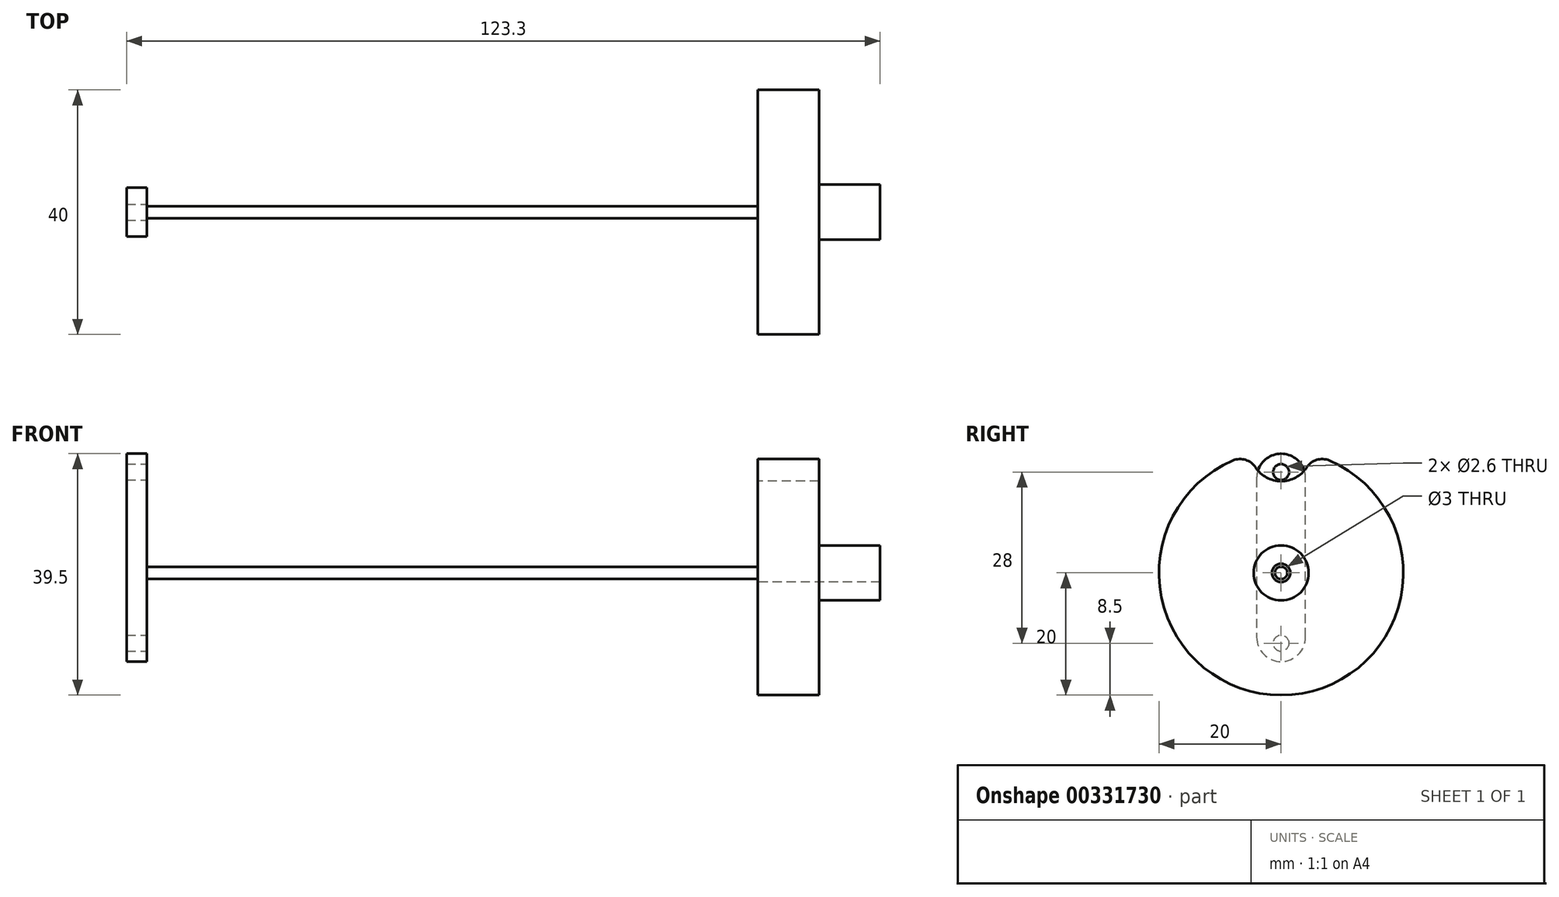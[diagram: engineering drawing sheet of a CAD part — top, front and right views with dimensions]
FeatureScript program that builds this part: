
annotation { "Feature Type Name" : "Feature", "Feature Type Description" : "" }
export const myFeature = defineFeature(function(context is Context, id is Id, definition is map)
    precondition{}
    {
        {
            var Q0;
            Q0=qCreatedBy(makeId("Right.planeOp"),FACE);
            var sketch = newSketch(context, id + "F0", { "sketchPlane" : qUnion([Q0])});
            skCircle(sketch, "E0", {"center": v(0, 0) * mm, "radius": 1 * mm});
            skSolve(sketch);
        }
        {
            var Q0;
            Q0 = qSketchRegion(id + "F0", true);
            extrude(context, id + "F1", {"entities" : qUnion([Q0]), "depth" : 100 * mm});
        }
        {
            var Q0;
            Q0=qCreatedBy(makeId("Right.planeOp"),FACE);
            var sketch = newSketch(context, id + "F2", { "sketchPlane" : qUnion([Q0])});
            skLineSegment(sketch, "E1", {"start": v(0, 0) * mm, "end": v(0, 16.5) * mm, "construction": true});
            skLineSegment(sketch, "E2", {"start": v(0, 0) * mm, "end": v(0, -11.5) * mm, "construction": true});
            skCircle(sketch, "E3", {"center": v(0, 16.5) * mm, "radius": 1.3 * mm});
            skCircle(sketch, "E4", {"center": v(0, -11.5) * mm, "radius": 1.3 * mm});
            skLineSegment(sketch, "E5", {"start": v(0, 16.5) * mm, "end": v(-4, 16.5) * mm, "construction": true});
            skLineSegment(sketch, "E6", {"start": v(-4, 15.5) * mm, "end": v(-4, -10.5) * mm, "construction": true});
            skLineSegment(sketch, "E7", {"start": v(-4, -11.5) * mm, "end": v(4, -11.5) * mm, "construction": true});
            skLineSegment(sketch, "E8", {"start": v(4, -10.5) * mm, "end": v(4, 15.5) * mm, "construction": true});
            skLineSegment(sketch, "E9", {"start": v(4, 16.5) * mm, "end": v(0, 16.5) * mm, "construction": true});
            skLineSegment(sketch, "E10", {"start": v(4, -10.5) * mm, "end": v(4, 15.5) * mm});
            skLineSegment(sketch, "E11", {"start": v(-4, 15.5) * mm, "end": v(-4, -10.5) * mm});
            skLineSegment(sketch, "E12", {"start": v(0, 19.5) * mm, "end": v(0, 19.5) * mm});
            skPoint(sketch, "E13.visualSharp", {"position": v(4, 19.5) * mm});
            skArc(sketch, "E13.filletArc", {"start": v(4, 15.5) * mm, "mid": v(2.83, 18.33) * mm, "end": v(0, 19.5) * mm});
            skPoint(sketch, "E14.visualSharp", {"position": v(-4, 19.5) * mm});
            skArc(sketch, "E14.filletArc", {"start": v(0, 19.5) * mm, "mid": v(-2.83, 18.33) * mm, "end": v(-4, 15.5) * mm});
            skLineSegment(sketch, "E15", {"start": v(0, -14.5) * mm, "end": v(0, -14.5) * mm});
            skPoint(sketch, "E16.visualSharp", {"position": v(4, -14.5) * mm});
            skArc(sketch, "E16.filletArc", {"start": v(0, -14.5) * mm, "mid": v(2.83, -13.33) * mm, "end": v(4, -10.5) * mm});
            skPoint(sketch, "E17.visualSharp", {"position": v(-4, -14.5) * mm});
            skArc(sketch, "E17.filletArc", {"start": v(-4, -10.5) * mm, "mid": v(-2.83, -13.33) * mm, "end": v(0, -14.5) * mm});
            skSolve(sketch);
        }
        {
            var Q0;
            Q0 = qSketchRegion(id + "F2", true);
            extrude(context, id + "F3", {"entities" : qUnion([Q0]), "operationType" : NewBodyOperationType.ADD, "oppositeDirection" : true, "depth" : 3.3 * mm});
        }
        {
            var Q0;
            Q0=makeQuery(id+"F1.opExtrude","CAP_FACE",FACE,{"disambiguationData":[OSD([sQuery(id+"F0.wireOp",EDGE,"E0")])],"isStart":false});
            var sketch = newSketch(context, id + "F4", { "sketchPlane" : qUnion([Q0])});
            skArc(sketch, "E18", {"start": v(-7.88, 18.38) * mm, "mid": v(0, -20) * mm, "end": v(7.88, 18.38) * mm});
            skCircle(sketch, "E19", {"center": v(0, 0) * mm, "radius": 1.5 * mm});
            skLineSegment(sketch, "E20", {"start": v(0, 20) * mm, "end": v(-5, 20) * mm, "construction": true});
            skLineSegment(sketch, "E21", {"start": v(0, 20) * mm, "end": v(5, 20) * mm, "construction": true});
            skArc(sketch, "E22", {"start": v(-5, 20) * mm, "mid": v(0, 15) * mm, "end": v(5, 20) * mm, "construction": true});
            skArc(sketch, "E23", {"start": v(-4.19, 17.27) * mm, "mid": v(0, 15) * mm, "end": v(4.19, 17.27) * mm});
            skPoint(sketch, "E24.visualSharp", {"position": v(-4.96, 19.37) * mm});
            skArc(sketch, "E24.filletArc", {"start": v(-4.19, 17.27) * mm, "mid": v(-5.83, 18.5) * mm, "end": v(-7.88, 18.38) * mm});
            skPoint(sketch, "E25.visualSharp", {"position": v(4.96, 19.37) * mm});
            skArc(sketch, "E25.filletArc", {"start": v(7.88, 18.38) * mm, "mid": v(5.83, 18.5) * mm, "end": v(4.19, 17.27) * mm});
            skSolve(sketch);
        }
        {
            var Q0;
            Q0=makeQuery(id+"F4.imprint","IMPRINT",FACE,{"disambiguationData":[TD([[makeQuery(id+"F4.imprint","IMPRINT",EDGE,{"derivedFrom":sQuery(id+"F4.wireOp",EDGE,"E18")}),1.0]])]});
            extrude(context, id + "F5", {"entities" : qUnion([Q0]), "depth" : 10 * mm});
        }
        {
            var Q0;
            Q0=makeQuery(id+"F5.opExtrude","CAP_FACE",FACE,{"disambiguationData":[OSD([sQuery(id+"F4.wireOp",EDGE,"E18"),sQuery(id+"F4.wireOp",EDGE,"E19"),sQuery(id+"F4.wireOp",EDGE,"E23"),sQuery(id+"F4.wireOp",EDGE,"E24.filletArc"),sQuery(id+"F4.wireOp",EDGE,"E25.filletArc")])],"isStart":false});
            var sketch = newSketch(context, id + "F6", { "sketchPlane" : qUnion([Q0])});
            skCircle(sketch, "E26", {"center": v(0, 0) * mm, "radius": 1.5 * mm});
            skCircle(sketch, "E27", {"center": v(0, 0) * mm, "radius": 4.5 * mm});
            skSolve(sketch);
        }
        {
            var Q0;
            Q0 = qSketchRegion(id + "F6", true);
            extrude(context, id + "F7", {"entities" : qUnion([Q0]), "operationType" : NewBodyOperationType.ADD, "depth" : 10 * mm});
        }
    });
